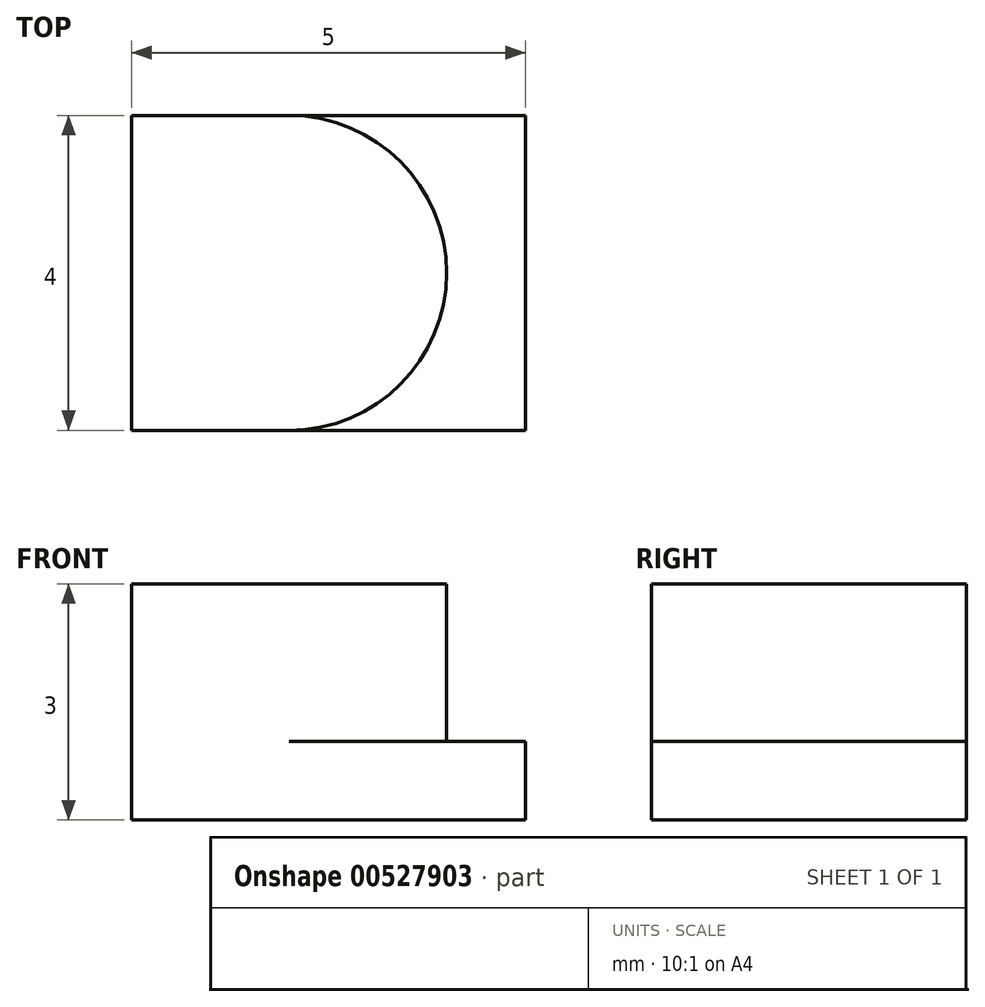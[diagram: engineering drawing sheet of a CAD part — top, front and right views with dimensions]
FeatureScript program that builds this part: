
annotation { "Feature Type Name" : "Feature", "Feature Type Description" : "" }
export const myFeature = defineFeature(function(context is Context, id is Id, definition is map)
    precondition{}
    {
        {
            var Q0;
            Q0=qCreatedBy(makeId("Top.planeOp"),FACE);
            var sketch = newSketch(context, id + "F0", { "sketchPlane" : qUnion([Q0])});
            skLineSegment(sketch, "E0.bottom", {"start": v(0, 0) * mm, "end": v(5, 0) * mm});
            skLineSegment(sketch, "E0.top", {"start": v(0, 4) * mm, "end": v(5, 4) * mm});
            skLineSegment(sketch, "E0.left", {"start": v(0, 0) * mm, "end": v(0, 4) * mm});
            skLineSegment(sketch, "E0.right", {"start": v(5, 0) * mm, "end": v(5, 4) * mm});
            skSolve(sketch);
        }
        {
            var Q0;
            Q0=qSketchRegion(id+"F0",true);
            extrude(context, id + "F1", {"entities" : qUnion([Q0]), "depth" : 1 * mm});
        }
        {
            var Q0;
            Q0=makeQuery(id+"F1.opExtrude","CAP_FACE",FACE,{"disambiguationData":[OSD([sQuery(id+"F0.wireOp",EDGE,"E0.bottom"),sQuery(id+"F0.wireOp",EDGE,"E0.top"),sQuery(id+"F0.wireOp",EDGE,"E0.left"),sQuery(id+"F0.wireOp",EDGE,"E0.right")])],"isStart":false});
            var sketch = newSketch(context, id + "F2", { "sketchPlane" : qUnion([Q0])});
            skLineSegment(sketch, "E1", {"start": v(0, 2) * mm, "end": v(2, 2) * mm, "construction": true});
            skArc(sketch, "E2", {"start": v(2, 0) * mm, "mid": v(4, 2) * mm, "end": v(2, 4) * mm});
            skLineSegment(sketch, "E3.0", {"start": v(0, 4) * mm, "end": v(2, 4) * mm});
            skLineSegment(sketch, "E3.1", {"start": v(0, 0) * mm, "end": v(2, 0) * mm});
            skLineSegment(sketch, "E3.2", {"start": v(0, 0) * mm, "end": v(0, 4) * mm});
            skSolve(sketch);
        }
        {
            var Q0;
            Q0=qSketchRegion(id+"F2",true);
            extrude(context, id + "F3", {"entities" : qUnion([Q0]), "operationType" : NewBodyOperationType.ADD, "depth" : 2 * mm});
        }
    });
